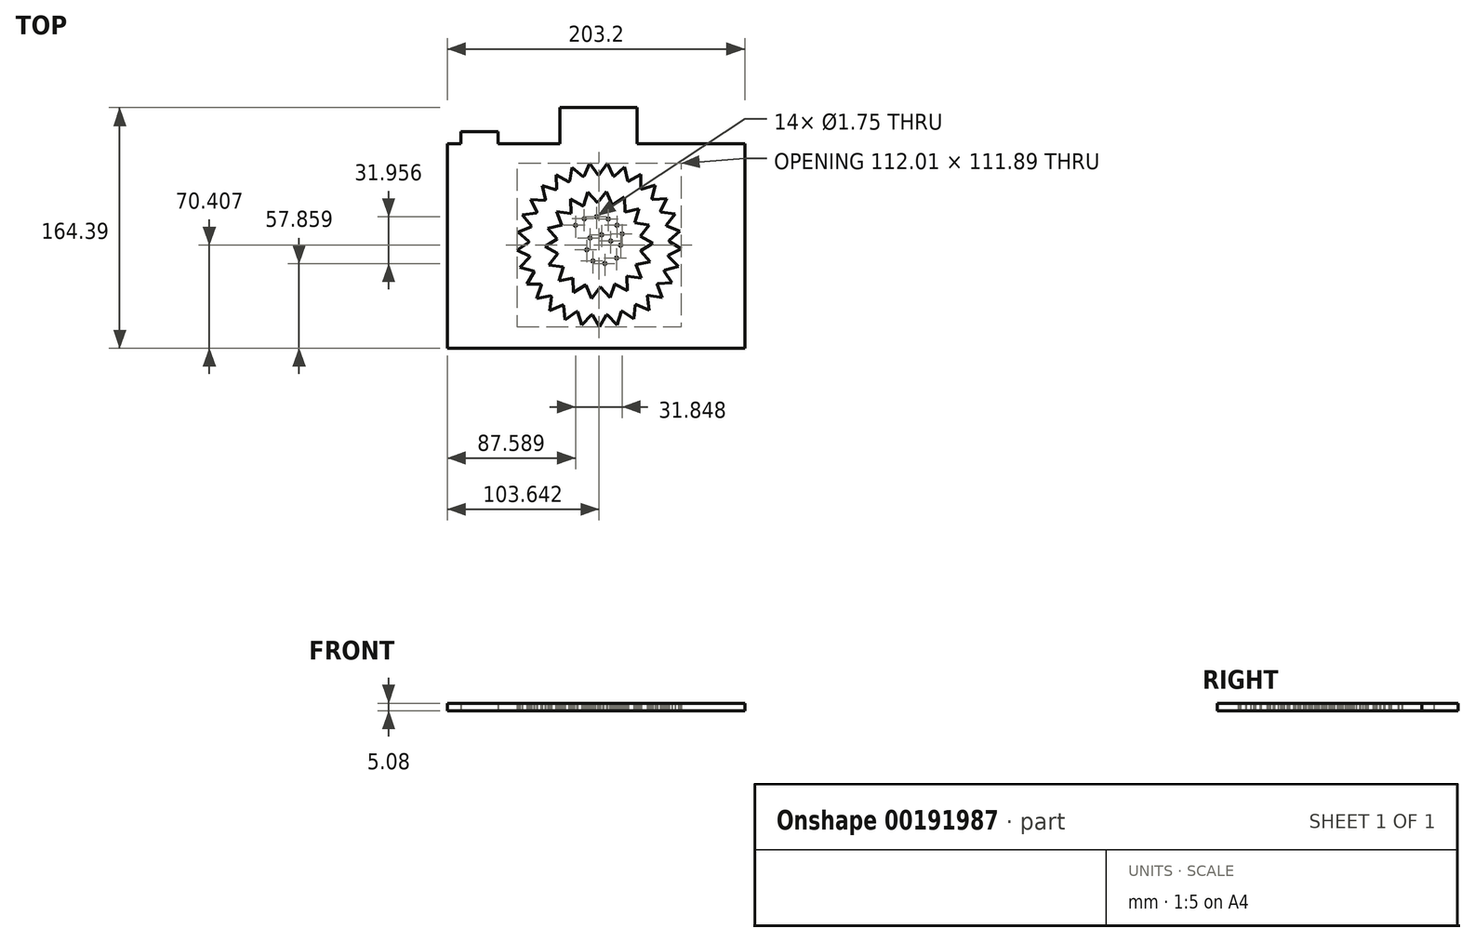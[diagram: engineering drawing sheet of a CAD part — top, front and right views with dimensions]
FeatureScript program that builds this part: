
annotation { "Feature Type Name" : "Feature", "Feature Type Description" : "" }
export const myFeature = defineFeature(function(context is Context, id is Id, definition is map)
    precondition{}
    {
        {
            var Q0;
            Q0=qCreatedBy(makeId("Top.planeOp"),FACE);
            var sketch = newSketch(context, id + "F0", { "sketchPlane" : qUnion([Q0])});
            skCircle(sketch, "E0", {"center": v(0, 0) * mm, "radius": 47.93 * mm});
            skLineSegment(sketch, "E1", {"start": v(0, 47.93) * mm, "end": v(5.66, 55.8) * mm});
            skLineSegment(sketch, "E2", {"start": v(5.66, 55.8) * mm, "end": v(9.68, 46.94) * mm});
            skLineSegment(sketch, "E3.1.0", {"start": v(-10.3, 46.81) * mm, "end": v(-6.46, 55.71) * mm});
            skLineSegment(sketch, "E3.1.1", {"start": v(-6.46, 55.71) * mm, "end": v(-0.63, 47.93) * mm});
            skLineSegment(sketch, "E3.2.0", {"start": v(-20.13, 43.5) * mm, "end": v(-18.29, 53.02) * mm});
            skLineSegment(sketch, "E3.2.1", {"start": v(-18.29, 53.02) * mm, "end": v(-10.92, 46.67) * mm});
            skLineSegment(sketch, "E4.1.3.0", {"start": v(-29, 38.16) * mm, "end": v(-29.26, 47.85) * mm});
            skLineSegment(sketch, "E4.3.3.0", {"start": v(-29.26, 47.85) * mm, "end": v(-20.7, 43.23) * mm});
            skLineSegment(sketch, "E4.1.4.0", {"start": v(-36.53, 31.03) * mm, "end": v(-38.86, 40.44) * mm});
            skLineSegment(sketch, "E4.3.4.0", {"start": v(-38.86, 40.44) * mm, "end": v(-29.5, 37.77) * mm});
            skLineSegment(sketch, "E4.1.5.0", {"start": v(-42.35, 22.45) * mm, "end": v(-46.65, 31.14) * mm});
            skLineSegment(sketch, "E4.3.5.0", {"start": v(-46.65, 31.14) * mm, "end": v(-36.94, 30.54) * mm});
            skArc(sketch, "E4.6.5.0", {"start": v(-46.35, 12.22) * mm, "mid": v(46.27, -12.52) * mm, "end": v(-46.18, 12.82) * mm});
            skLineSegment(sketch, "E4.1.6.0", {"start": v(-46.18, 12.82) * mm, "end": v(-52.25, 20.39) * mm});
            skLineSegment(sketch, "E4.3.6.0", {"start": v(-52.25, 20.39) * mm, "end": v(-42.64, 21.89) * mm});
            skLineSegment(sketch, "E4.1.7.0", {"start": v(-47.86, 2.6) * mm, "end": v(-55.41, 8.68) * mm});
            skLineSegment(sketch, "E4.3.7.0", {"start": v(-55.41, 8.68) * mm, "end": v(-46.35, 12.21) * mm});
            skLineSegment(sketch, "E4.1.8.0", {"start": v(-47.3, -7.75) * mm, "end": v(-55.98, -3.44) * mm});
            skLineSegment(sketch, "E4.3.8.0", {"start": v(-55.98, -3.44) * mm, "end": v(-47.9, 1.96) * mm});
            skArc(sketch, "E4.6.8.0", {"start": v(0, 47.93) * mm, "mid": v(-4.87, -47.68) * mm, "end": v(9.68, 46.94) * mm});
            skLineSegment(sketch, "E4.1.9.0", {"start": v(-44.53, -17.74) * mm, "end": v(-53.93, -15.4) * mm});
            skLineSegment(sketch, "E4.3.9.0", {"start": v(-53.93, -15.4) * mm, "end": v(-47.2, -8.38) * mm});
            skLineSegment(sketch, "E4.1.10.0", {"start": v(-39.67, -26.9) * mm, "end": v(-49.36, -26.63) * mm});
            skLineSegment(sketch, "E4.3.10.0", {"start": v(-49.36, -26.63) * mm, "end": v(-44.29, -18.33) * mm});
            skArc(sketch, "E4.6.10.0", {"start": v(-46.35, 12.22) * mm, "mid": v(46.27, -12.52) * mm, "end": v(-46.18, 12.82) * mm});
            skLineSegment(sketch, "E4.1.11.0", {"start": v(-32.96, -34.8) * mm, "end": v(-42.49, -36.62) * mm});
            skLineSegment(sketch, "E4.3.11.0", {"start": v(-42.49, -36.62) * mm, "end": v(-39.31, -27.42) * mm});
            skLineSegment(sketch, "E4.1.12.0", {"start": v(-24.71, -41.07) * mm, "end": v(-33.62, -44.9) * mm});
            skLineSegment(sketch, "E4.3.12.0", {"start": v(-33.62, -44.9) * mm, "end": v(-32.5, -35.23) * mm});
            skLineSegment(sketch, "E4.1.13.0", {"start": v(-15.3, -45.42) * mm, "end": v(-23.19, -51.07) * mm});
            skLineSegment(sketch, "E4.3.13.0", {"start": v(-23.19, -51.07) * mm, "end": v(-24.16, -41.4) * mm});
            skLineSegment(sketch, "E4.1.14.0", {"start": v(-5.18, -47.65) * mm, "end": v(-11.66, -54.86) * mm});
            skLineSegment(sketch, "E4.3.14.0", {"start": v(-11.66, -54.86) * mm, "end": v(-14.7, -45.62) * mm});
            skLineSegment(sketch, "E4.1.15.0", {"start": v(5.18, -47.65) * mm, "end": v(0.4, -56.09) * mm});
            skLineSegment(sketch, "E4.3.15.0", {"start": v(0.4, -56.09) * mm, "end": v(-4.55, -47.71) * mm});
            skLineSegment(sketch, "E4.1.16.0", {"start": v(15.3, -45.42) * mm, "end": v(12.45, -54.69) * mm});
            skLineSegment(sketch, "E4.3.16.0", {"start": v(12.45, -54.69) * mm, "end": v(5.81, -47.58) * mm});
            skLineSegment(sketch, "E4.1.17.0", {"start": v(24.71, -41.07) * mm, "end": v(23.91, -50.73) * mm});
            skLineSegment(sketch, "E4.3.17.0", {"start": v(23.91, -50.73) * mm, "end": v(15.9, -45.22) * mm});
            skLineSegment(sketch, "E4.1.18.0", {"start": v(32.96, -34.8) * mm, "end": v(34.26, -44.4) * mm});
            skLineSegment(sketch, "E4.3.18.0", {"start": v(34.26, -44.4) * mm, "end": v(25.25, -40.74) * mm});
            skLineSegment(sketch, "E4.1.19.0", {"start": v(39.67, -26.9) * mm, "end": v(43, -36) * mm});
            skLineSegment(sketch, "E4.3.19.0", {"start": v(43, -36) * mm, "end": v(33.42, -34.36) * mm});
            skArc(sketch, "E4.6.19.0", {"start": v(0, 47.93) * mm, "mid": v(-4.87, -47.68) * mm, "end": v(9.68, 46.94) * mm});
            skLineSegment(sketch, "E4.1.20.0", {"start": v(44.53, -17.74) * mm, "end": v(49.74, -25.92) * mm});
            skLineSegment(sketch, "E4.3.20.0", {"start": v(49.74, -25.92) * mm, "end": v(40.03, -26.37) * mm});
            skLineSegment(sketch, "E4.1.21.0", {"start": v(47.3, -7.75) * mm, "end": v(54.15, -14.62) * mm});
            skLineSegment(sketch, "E4.3.21.0", {"start": v(54.15, -14.62) * mm, "end": v(44.76, -17.15) * mm});
            skLineSegment(sketch, "E4.1.22.0", {"start": v(47.86, 2.6) * mm, "end": v(56.03, -2.64) * mm});
            skLineSegment(sketch, "E4.3.22.0", {"start": v(56.03, -2.64) * mm, "end": v(47.4, -7.13) * mm});
            skLineSegment(sketch, "E4.1.23.0", {"start": v(46.18, 12.82) * mm, "end": v(55.28, 9.47) * mm});
            skLineSegment(sketch, "E4.3.23.0", {"start": v(55.28, 9.47) * mm, "end": v(47.82, 3.23) * mm});
            skLineSegment(sketch, "E4.1.24.0", {"start": v(42.35, 22.45) * mm, "end": v(51.95, 21.13) * mm});
            skLineSegment(sketch, "E4.3.24.0", {"start": v(51.95, 21.13) * mm, "end": v(46.01, 13.43) * mm});
            skArc(sketch, "E4.6.24.0", {"start": v(0, 47.93) * mm, "mid": v(-4.87, -47.68) * mm, "end": v(9.68, 46.94) * mm});
            skLineSegment(sketch, "E4.1.25.0", {"start": v(36.53, 31.03) * mm, "end": v(46.2, 31.8) * mm});
            skLineSegment(sketch, "E4.3.25.0", {"start": v(46.2, 31.8) * mm, "end": v(42.05, 23.01) * mm});
            skLineSegment(sketch, "E4.1.26.0", {"start": v(29, 38.16) * mm, "end": v(38.28, 41) * mm});
            skLineSegment(sketch, "E4.3.26.0", {"start": v(38.28, 41) * mm, "end": v(36.12, 31.51) * mm});
            skLineSegment(sketch, "E4.1.27.0", {"start": v(20.13, 43.5) * mm, "end": v(28.57, 48.26) * mm});
            skLineSegment(sketch, "E4.3.27.0", {"start": v(28.57, 48.26) * mm, "end": v(28.5, 38.54) * mm});
            skLineSegment(sketch, "E4.1.28.0", {"start": v(10.3, 46.81) * mm, "end": v(17.53, 53.28) * mm});
            skLineSegment(sketch, "E4.3.28.0", {"start": v(17.53, 53.28) * mm, "end": v(19.55, 43.76) * mm});
            skArc(sketch, "E5.trimOffspring", {"start": v(0, 47.93) * mm, "mid": v(-0.32, 47.93) * mm, "end": v(-0.63, 47.93) * mm});
            skArc(sketch, "E6.trimOffspring", {"start": v(-29, 38.16) * mm, "mid": v(-39.67, 26.9) * mm, "end": v(-46.18, 12.82) * mm});
            skArc(sketch, "E7.trimOffspring", {"start": v(-20.13, 43.5) * mm, "mid": v(-20.41, 43.37) * mm, "end": v(-20.7, 43.23) * mm});
            skLineSegment(sketch, "E8.bottom", {"start": v(-103.62, 69.15) * mm, "end": v(-94.39, 69.15) * mm});
            skLineSegment(sketch, "E8.top", {"start": v(-103.62, -70.55) * mm, "end": v(99.58, -70.55) * mm});
            skLineSegment(sketch, "E8.left", {"start": v(-103.62, 69.15) * mm, "end": v(-103.62, -70.55) * mm});
            skLineSegment(sketch, "E8.right", {"start": v(99.58, 69.15) * mm, "end": v(99.58, -70.55) * mm});
            skLineSegment(sketch, "E9.bottom", {"start": v(-26.73, 93.84) * mm, "end": v(26.1, 93.84) * mm});
            skLineSegment(sketch, "E9.left", {"start": v(-26.73, 93.84) * mm, "end": v(-26.73, 69.15) * mm});
            skLineSegment(sketch, "E9.right", {"start": v(26.1, 93.84) * mm, "end": v(26.1, 69.15) * mm});
            skLineSegment(sketch, "E10.trimOffspring", {"start": v(26.1, 69.15) * mm, "end": v(99.58, 69.15) * mm});
            skLineSegment(sketch, "E11.bottom", {"start": v(-94.39, 77.35) * mm, "end": v(-68.99, 77.35) * mm});
            skLineSegment(sketch, "E11.left", {"start": v(-94.39, 77.35) * mm, "end": v(-94.39, 69.15) * mm});
            skLineSegment(sketch, "E11.right", {"start": v(-68.99, 77.35) * mm, "end": v(-68.99, 69.15) * mm});
            skLineSegment(sketch, "E12", {"start": v(-68.99, 69.15) * mm, "end": v(-26.73, 69.15) * mm});
            skArc(sketch, "E13", {"start": v(-46.18, 12.82) * mm, "mid": v(-46.27, 12.52) * mm, "end": v(-46.35, 12.22) * mm});
            skArc(sketch, "E14", {"start": v(-46.35, 12.22) * mm, "mid": v(25.25, -40.74) * mm, "end": v(9.68, 46.94) * mm});
            skSolve(sketch);
        }
        {
            var Q0;
            {var subQ41=sQuery(id+"F0.wireOp",EDGE,"E1");Q0=makeQuery(id+"F0.imprint","IMPRINT",FACE,{"disambiguationData":[TD([[makeQuery(id+"F0.imprint","IMPRINT",EDGE,{"derivedFrom":subQ41}),1.0]])]});}
            extrude(context, id + "F1", {"entities" : qUnion([Q0]), "depth" : 5.08 * mm});
        }
        {
            var Q0;
            Q0=qCreatedBy(makeId("Top.planeOp"),FACE);
            var sketch = newSketch(context, id + "F2", { "sketchPlane" : qUnion([Q0])});
            skCircle(sketch, "E15", {"center": v(0, 0) * mm, "radius": 28.79 * mm});
            skLineSegment(sketch, "E16", {"start": v(-25.34, 13.67) * mm, "end": v(-28.97, 22.75) * mm});
            skLineSegment(sketch, "E17", {"start": v(-28.97, 22.75) * mm, "end": v(-19.29, 21.37) * mm});
            skLineSegment(sketch, "E18.1.0", {"start": v(-35, 11.47) * mm, "end": v(-25.43, 13.48) * mm});
            skLineSegment(sketch, "E18.1.1", {"start": v(-28.48, 4.18) * mm, "end": v(-35, 11.47) * mm});
            skLineSegment(sketch, "E18.2.0", {"start": v(-36.81, -1.2) * mm, "end": v(-28.51, 3.97) * mm});
            skLineSegment(sketch, "E18.2.1", {"start": v(-28.2, -5.82) * mm, "end": v(-36.81, -1.2) * mm});
            skLineSegment(sketch, "E18.3.0", {"start": v(-34.18, -13.72) * mm, "end": v(-28.15, -6.02) * mm});
            skLineSegment(sketch, "E18.3.1", {"start": v(-24.5, -15.1) * mm, "end": v(-34.18, -13.72) * mm});
            skLineSegment(sketch, "E18.4.0", {"start": v(-27.43, -24.58) * mm, "end": v(-24.4, -15.28) * mm});
            skLineSegment(sketch, "E18.4.1", {"start": v(-17.86, -22.58) * mm, "end": v(-27.43, -24.58) * mm});
            skLineSegment(sketch, "E18.5.0", {"start": v(-17.37, -32.48) * mm, "end": v(-17.7, -22.7) * mm});
            skLineSegment(sketch, "E18.5.1", {"start": v(-9.06, -27.32) * mm, "end": v(-17.37, -32.48) * mm});
            skLineSegment(sketch, "E18.6.0", {"start": v(-5.21, -36.46) * mm, "end": v(-8.86, -27.39) * mm});
            skLineSegment(sketch, "E18.6.1", {"start": v(0.83, -28.78) * mm, "end": v(-5.21, -36.46) * mm});
            skLineSegment(sketch, "E18.7.0", {"start": v(7.57, -36.05) * mm, "end": v(1.04, -28.77) * mm});
            skLineSegment(sketch, "E18.7.1", {"start": v(10.62, -26.76) * mm, "end": v(7.57, -36.05) * mm});
            skLineSegment(sketch, "E18.8.0", {"start": v(19.44, -31.28) * mm, "end": v(10.82, -26.68) * mm});
            skLineSegment(sketch, "E18.8.1", {"start": v(19.13, -21.5) * mm, "end": v(19.44, -31.28) * mm});
            skLineSegment(sketch, "E18.9.0", {"start": v(28.97, -22.75) * mm, "end": v(19.29, -21.37) * mm});
            skLineSegment(sketch, "E18.9.1", {"start": v(25.34, -13.67) * mm, "end": v(28.97, -22.75) * mm});
            skLineSegment(sketch, "E18.10.0", {"start": v(35, -11.47) * mm, "end": v(25.43, -13.48) * mm});
            skLineSegment(sketch, "E18.10.1", {"start": v(28.48, -4.18) * mm, "end": v(35, -11.47) * mm});
            skLineSegment(sketch, "E18.11.0", {"start": v(36.81, 1.2) * mm, "end": v(28.51, -3.97) * mm});
            skLineSegment(sketch, "E18.11.1", {"start": v(28.2, 5.82) * mm, "end": v(36.81, 1.2) * mm});
            skLineSegment(sketch, "E18.12.0", {"start": v(34.18, 13.72) * mm, "end": v(28.15, 6.02) * mm});
            skLineSegment(sketch, "E18.12.1", {"start": v(24.5, 15.1) * mm, "end": v(34.18, 13.72) * mm});
            skLineSegment(sketch, "E18.13.0", {"start": v(27.43, 24.58) * mm, "end": v(24.4, 15.28) * mm});
            skLineSegment(sketch, "E18.13.1", {"start": v(17.86, 22.58) * mm, "end": v(27.43, 24.58) * mm});
            skLineSegment(sketch, "E18.14.0", {"start": v(17.37, 32.48) * mm, "end": v(17.7, 22.7) * mm});
            skLineSegment(sketch, "E18.14.1", {"start": v(9.06, 27.32) * mm, "end": v(17.37, 32.48) * mm});
            skLineSegment(sketch, "E19.3.15.0", {"start": v(-0.83, 28.78) * mm, "end": v(5.21, 36.46) * mm});
            skLineSegment(sketch, "E19.4.15.0", {"start": v(5.21, 36.46) * mm, "end": v(8.86, 27.39) * mm});
            skLineSegment(sketch, "E19.3.16.0", {"start": v(-10.62, 26.76) * mm, "end": v(-7.57, 36.05) * mm});
            skLineSegment(sketch, "E19.4.16.0", {"start": v(-7.57, 36.05) * mm, "end": v(-1.04, 28.77) * mm});
            skLineSegment(sketch, "E19.3.17.0", {"start": v(-19.13, 21.5) * mm, "end": v(-19.44, 31.28) * mm});
            skLineSegment(sketch, "E19.4.17.0", {"start": v(-19.44, 31.28) * mm, "end": v(-10.82, 26.68) * mm});
            skCircle(sketch, "E20", {"center": v(-16.03, 13.4) * mm, "radius": 0.87 * mm});
            skCircle(sketch, "E21", {"center": v(-10.06, 17.88) * mm, "radius": 0.87 * mm});
            skCircle(sketch, "E22", {"center": v(-1.64, 19.27) * mm, "radius": 0.87 * mm});
            skCircle(sketch, "E23", {"center": v(6.35, 17.72) * mm, "radius": 0.87 * mm});
            skCircle(sketch, "E24", {"center": v(15.82, 7.54) * mm, "radius": 0.87 * mm});
            skCircle(sketch, "E25", {"center": v(14.82, -0.16) * mm, "radius": 0.87 * mm});
            skCircle(sketch, "E26", {"center": v(4.05, -12.7) * mm, "radius": 0.87 * mm});
            skCircle(sketch, "E27", {"center": v(-8.3, -3.34) * mm, "radius": 0.87 * mm});
            skCircle(sketch, "E28", {"center": v(-4.18, -10.95) * mm, "radius": 0.87 * mm});
            skCircle(sketch, "E29", {"center": v(-6.08, 4.74) * mm, "radius": 0.87 * mm});
            skCircle(sketch, "E30", {"center": v(1.8, 6.9) * mm, "radius": 0.87 * mm});
            skCircle(sketch, "E31", {"center": v(8.03, 2.71) * mm, "radius": 0.87 * mm});
            skCircle(sketch, "E32", {"center": v(12.34, 13.44) * mm, "radius": 0.87 * mm});
            skCircle(sketch, "E33", {"center": v(12, -8.96) * mm, "radius": 0.87 * mm});
            skSolve(sketch);
        }
        {
            var Q0;
            Q0 = qSketchRegion(id + "F2", true);
            extrude(context, id + "F3", {"entities" : qUnion([Q0]), "operationType" : NewBodyOperationType.ADD, "depth" : 5.08 * mm});
        }
    });
